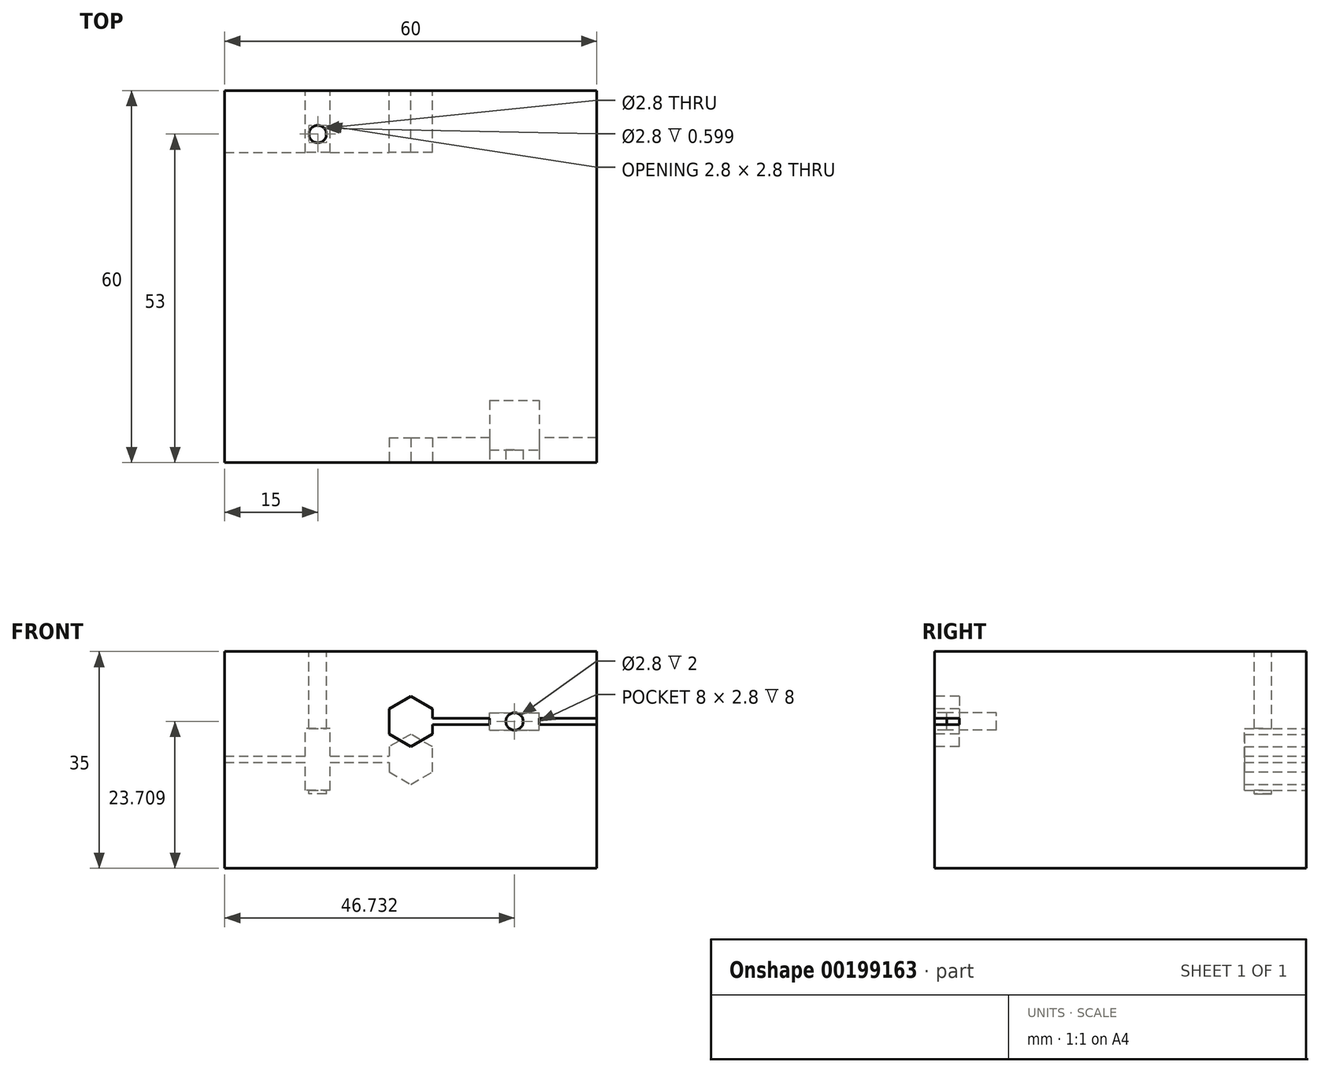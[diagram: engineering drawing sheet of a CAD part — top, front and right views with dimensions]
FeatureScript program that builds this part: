
annotation { "Feature Type Name" : "Feature", "Feature Type Description" : "" }
export const myFeature = defineFeature(function(context is Context, id is Id, definition is map)
    precondition{}
    {
        {
            var Q0;
            Q0=qCreatedBy(makeId("Top.planeOp"),FACE);
            var sketch = newSketch(context, id + "F0", { "sketchPlane" : qUnion([Q0])});
            skLineSegment(sketch, "E0.bottom", {"start": v(-30, -30) * mm, "end": v(30, -30) * mm});
            skLineSegment(sketch, "E0.top", {"start": v(-30, 30) * mm, "end": v(30, 30) * mm});
            skLineSegment(sketch, "E0.left", {"start": v(-30, -30) * mm, "end": v(-30, 30) * mm});
            skLineSegment(sketch, "E0.right", {"start": v(30, -30) * mm, "end": v(30, 30) * mm});
            skPoint(sketch, "E0.middle", {"position": v(0, 0) * mm});
            skSolve(sketch);
        }
        {
            var Q0;
            Q0=makeQuery(id+"F0.imprint","IMPRINT",FACE,{"disambiguationData":[TD([[makeQuery(id+"F0.imprint","IMPRINT",EDGE,{"derivedFrom":sQuery(id+"F0.wireOp",EDGE,"E0.bottom")}),1.0]])]});
            extrude(context, id + "F1", {"entities" : qUnion([Q0]), "depth" : 35 * mm});
        }
        {
            var Q0;
            Q0=makeQuery(id+"F1.opExtrude","SWEPT_FACE",FACE,{"disambiguationData":[OSD([sQuery(id+"F0.wireOp",EDGE,"E0.bottom")])]});
            var sketch = newSketch(context, id + "F2", { "sketchPlane" : qUnion([Q0])});
            skLineSegment(sketch, "E1.bottom", {"start": v(30, 24.2) * mm, "end": v(18.04, 24.2) * mm});
            skLineSegment(sketch, "E1.top", {"start": v(30, 23.2) * mm, "end": v(18.04, 23.2) * mm});
            skLineSegment(sketch, "E1.left", {"start": v(30, 24.2) * mm, "end": v(30, 23.2) * mm});
            skCircle(sketch, "E2", {"center": v(0, 23.7) * mm, "radius": 3.5 * mm});
            skCircle(sketch, "E3.cCircle", {"center": v(0, 23.7) * mm, "radius": 3.5 * mm, "construction": true});
            skLineSegment(sketch, "E3.0", {"start": v(-3.5, 21.69) * mm, "end": v(-3.5, 25.73) * mm});
            skLineSegment(sketch, "E3.1", {"start": v(-3.5, 25.73) * mm, "end": v(0, 27.75) * mm});
            skLineSegment(sketch, "E3.2", {"start": v(0, 27.75) * mm, "end": v(3.5, 25.73) * mm});
            skLineSegment(sketch, "E3.3", {"start": v(3.5, 25.73) * mm, "end": v(3.5, 21.69) * mm});
            skLineSegment(sketch, "E3.4", {"start": v(3.5, 21.69) * mm, "end": v(0, 19.67) * mm});
            skLineSegment(sketch, "E3.5", {"start": v(0, 19.67) * mm, "end": v(-3.5, 21.69) * mm});
            skPoint(sketch, "E3.0.midPoint", {"position": v(-3.5, 23.7) * mm});
            skCircle(sketch, "E4", {"center": v(16.73, 23.7) * mm, "radius": 1.4 * mm});
            skLineSegment(sketch, "E5.bottom", {"start": v(12.73, 22.3) * mm, "end": v(20.73, 22.3) * mm});
            skLineSegment(sketch, "E5.top", {"start": v(12.73, 25.1) * mm, "end": v(20.73, 25.1) * mm});
            skLineSegment(sketch, "E5.left", {"start": v(12.73, 22.3) * mm, "end": v(12.73, 25.1) * mm});
            skLineSegment(sketch, "E5.right", {"start": v(20.73, 22.3) * mm, "end": v(20.73, 25.1) * mm});
            skLineSegment(sketch, "E6.trimOffspring", {"start": v(15.42, 23.2) * mm, "end": v(3.46, 23.2) * mm});
            skLineSegment(sketch, "E7.trimOffspring", {"start": v(15.42, 24.2) * mm, "end": v(3.46, 24.2) * mm});
            skSolve(sketch);
        }
        {
            var Q0;
            {var subQ0=sQuery(id+"F2.wireOp",EDGE,"E7.trimOffspring");var subQ1=sQuery(id+"F2.wireOp",EDGE,"E4");var subQ2=makeQuery(id+"F2.imprint","INTERSECT",VERTEX,{"derivedFrom":[subQ1,subQ0]});Q0=makeQuery(id+"F2.imprint","IMPRINT",FACE,{"disambiguationData":[TD([[makeQuery(id+"F2.imprint","IMPRINT",EDGE,{"disambiguationData":[TD([[subQ2,1.0]])],"derivedFrom":subQ1}),-1.0]])]});}
            var Q1;
            {var subQ0=sQuery(id+"F2.wireOp",EDGE,"E6.trimOffspring");var subQ1=sQuery(id+"F2.wireOp",EDGE,"E4");var subQ2=makeQuery(id+"F2.imprint","INTERSECT",VERTEX,{"derivedFrom":[subQ1,subQ0]});Q1=makeQuery(id+"F2.imprint","IMPRINT",FACE,{"disambiguationData":[TD([[makeQuery(id+"F2.imprint","IMPRINT",EDGE,{"disambiguationData":[TD([[subQ2,1.0]])],"derivedFrom":subQ1}),-1.0]])]});}
            var Q2;
            {var subQ0=sQuery(id+"F2.wireOp",EDGE,"E6.trimOffspring");var subQ1=sQuery(id+"F2.wireOp",EDGE,"E4");var subQ2=makeQuery(id+"F2.imprint","INTERSECT",VERTEX,{"derivedFrom":[subQ1,subQ0]});Q2=makeQuery(id+"F2.imprint","IMPRINT",FACE,{"disambiguationData":[TD([[makeQuery(id+"F2.imprint","IMPRINT",EDGE,{"disambiguationData":[TD([[subQ2,-1.0]])],"derivedFrom":subQ1}),-1.0]])]});}
            var Q3;
            {var subQ0=sQuery(id+"F2.wireOp",EDGE,"E4");var subQ3=makeQuery(id+"F2.imprint","INTERSECT",VERTEX,{"derivedFrom":[sQuery(id+"F2.wireOp",EDGE,"E1.bottom"),subQ0]});Q3=makeQuery(id+"F2.imprint","IMPRINT",FACE,{"disambiguationData":[TD([[makeQuery(id+"F2.imprint","IMPRINT",EDGE,{"disambiguationData":[TD([[subQ3,-1.0]])],"derivedFrom":subQ0}),1.0]])]});}
            var Q4;
            {var subQ0=sQuery(id+"F2.wireOp",EDGE,"E4");var subQ1=sQuery(id+"F2.wireOp",EDGE,"E1.bottom");var subQ2=makeQuery(id+"F2.imprint","INTERSECT",VERTEX,{"derivedFrom":[subQ1,subQ0]});Q4=makeQuery(id+"F2.imprint","IMPRINT",FACE,{"disambiguationData":[TD([[makeQuery(id+"F2.imprint","IMPRINT",EDGE,{"disambiguationData":[TD([[subQ2,1.0]])],"derivedFrom":subQ1}),-1.0]])]});}
            var Q5;
            {var subQ0=sQuery(id+"F2.wireOp",EDGE,"E4");var subQ1=sQuery(id+"F2.wireOp",EDGE,"E1.bottom");var subQ2=makeQuery(id+"F2.imprint","INTERSECT",VERTEX,{"derivedFrom":[subQ1,subQ0]});Q5=makeQuery(id+"F2.imprint","IMPRINT",FACE,{"disambiguationData":[TD([[makeQuery(id+"F2.imprint","IMPRINT",EDGE,{"disambiguationData":[TD([[subQ2,1.0]])],"derivedFrom":subQ1}),1.0]])]});}
            var Q6;
            {var subQ0=sQuery(id+"F2.wireOp",EDGE,"E4");var subQ1=sQuery(id+"F2.wireOp",EDGE,"E1.top");var subQ2=makeQuery(id+"F2.imprint","INTERSECT",VERTEX,{"derivedFrom":[subQ1,subQ0]});Q6=makeQuery(id+"F2.imprint","IMPRINT",FACE,{"disambiguationData":[TD([[makeQuery(id+"F2.imprint","IMPRINT",EDGE,{"disambiguationData":[TD([[subQ2,1.0]])],"derivedFrom":subQ1}),1.0]])]});}
            extrude(context, id + "F3", {"entities" : qUnion([Q0, Q1, Q2, Q3, Q4, Q5, Q6]), "operationType" : NewBodyOperationType.REMOVE, "oppositeDirection" : true, "depth" : 10 * mm});
        }
        {
            var Q0;
            Q0 = qSketchRegion(id + "F2", true);
            extrude(context, id + "F4", {"entities" : qUnion([Q0]), "operationType" : NewBodyOperationType.REMOVE, "oppositeDirection" : true, "depth" : 4 * mm});
        }
        {
            var Q0;
            {var subQ0=sQuery(id+"F2.wireOp",EDGE,"E4");var subQ1=sQuery(id+"F2.wireOp",EDGE,"E1.top");var subQ2=makeQuery(id+"F2.imprint","INTERSECT",VERTEX,{"derivedFrom":[subQ1,subQ0]});Q0=makeQuery(id+"F2.imprint","IMPRINT",FACE,{"disambiguationData":[TD([[makeQuery(id+"F2.imprint","IMPRINT",EDGE,{"disambiguationData":[TD([[subQ2,1.0]])],"derivedFrom":subQ1}),1.0]])]});}
            var Q1;
            {var subQ0=sQuery(id+"F2.wireOp",EDGE,"E7.trimOffspring");var subQ1=sQuery(id+"F2.wireOp",EDGE,"E4");var subQ2=makeQuery(id+"F2.imprint","INTERSECT",VERTEX,{"derivedFrom":[subQ1,subQ0]});Q1=makeQuery(id+"F2.imprint","IMPRINT",FACE,{"disambiguationData":[TD([[makeQuery(id+"F2.imprint","IMPRINT",EDGE,{"disambiguationData":[TD([[subQ2,1.0]])],"derivedFrom":subQ1}),-1.0]])]});}
            var Q2;
            {var subQ0=sQuery(id+"F2.wireOp",EDGE,"E6.trimOffspring");var subQ1=sQuery(id+"F2.wireOp",EDGE,"E4");var subQ2=makeQuery(id+"F2.imprint","INTERSECT",VERTEX,{"derivedFrom":[subQ1,subQ0]});Q2=makeQuery(id+"F2.imprint","IMPRINT",FACE,{"disambiguationData":[TD([[makeQuery(id+"F2.imprint","IMPRINT",EDGE,{"disambiguationData":[TD([[subQ2,-1.0]])],"derivedFrom":subQ1}),-1.0]])]});}
            var Q3;
            {var subQ0=sQuery(id+"F2.wireOp",EDGE,"E4");var subQ1=sQuery(id+"F2.wireOp",EDGE,"E1.bottom");var subQ2=makeQuery(id+"F2.imprint","INTERSECT",VERTEX,{"derivedFrom":[subQ1,subQ0]});Q3=makeQuery(id+"F2.imprint","IMPRINT",FACE,{"disambiguationData":[TD([[makeQuery(id+"F2.imprint","IMPRINT",EDGE,{"disambiguationData":[TD([[subQ2,1.0]])],"derivedFrom":subQ1}),1.0]])]});}
            var Q4;
            {var subQ0=sQuery(id+"F2.wireOp",EDGE,"E6.trimOffspring");var subQ1=sQuery(id+"F2.wireOp",EDGE,"E4");var subQ2=makeQuery(id+"F2.imprint","INTERSECT",VERTEX,{"derivedFrom":[subQ1,subQ0]});Q4=makeQuery(id+"F2.imprint","IMPRINT",FACE,{"disambiguationData":[TD([[makeQuery(id+"F2.imprint","IMPRINT",EDGE,{"disambiguationData":[TD([[subQ2,1.0]])],"derivedFrom":subQ1}),-1.0]])]});}
            var Q5;
            {var subQ0=sQuery(id+"F2.wireOp",EDGE,"E4");var subQ1=sQuery(id+"F2.wireOp",EDGE,"E1.bottom");var subQ2=makeQuery(id+"F2.imprint","INTERSECT",VERTEX,{"derivedFrom":[subQ1,subQ0]});Q5=makeQuery(id+"F2.imprint","IMPRINT",FACE,{"disambiguationData":[TD([[makeQuery(id+"F2.imprint","IMPRINT",EDGE,{"disambiguationData":[TD([[subQ2,1.0]])],"derivedFrom":subQ1}),-1.0]])]});}
            extrude(context, id + "F5", {"entities" : qUnion([Q0, Q1, Q2, Q3, Q4, Q5]), "operationType" : NewBodyOperationType.ADD, "oppositeDirection" : true, "depth" : 2 * mm});
        }
        {
            var Q0;
            Q0=makeQuery(id+"F1.opExtrude","SWEPT_FACE",FACE,{"disambiguationData":[OSD([sQuery(id+"F0.wireOp",EDGE,"E0.top")])]});
            var sketch = newSketch(context, id + "F6", { "sketchPlane" : qUnion([Q0])});
            skPoint(sketch, "E8", {"position": v(15, 17.6) * mm});
            skLineSegment(sketch, "E9.bottom", {"start": v(30, 17.1) * mm, "end": v(0, 17.1) * mm});
            skLineSegment(sketch, "E9.top", {"start": v(30, 18.1) * mm, "end": v(0, 18.1) * mm});
            skLineSegment(sketch, "E9.left", {"start": v(30, 17.1) * mm, "end": v(30, 18.1) * mm});
            skLineSegment(sketch, "E9.right", {"start": v(0, 17.1) * mm, "end": v(0, 18.1) * mm});
            skCircle(sketch, "E10", {"center": v(0, 17.6) * mm, "radius": 3.5 * mm});
            skCircle(sketch, "E11.cCircle", {"center": v(0, 17.6) * mm, "radius": 3.5 * mm, "construction": true});
            skLineSegment(sketch, "E11.0", {"start": v(-3.5, 15.58) * mm, "end": v(-3.5, 19.62) * mm});
            skLineSegment(sketch, "E11.1", {"start": v(-3.5, 19.62) * mm, "end": v(0, 21.64) * mm});
            skLineSegment(sketch, "E11.2", {"start": v(0, 21.64) * mm, "end": v(3.5, 19.62) * mm});
            skLineSegment(sketch, "E11.3", {"start": v(3.5, 19.62) * mm, "end": v(3.5, 15.58) * mm});
            skLineSegment(sketch, "E11.4", {"start": v(3.5, 15.58) * mm, "end": v(0, 13.56) * mm});
            skLineSegment(sketch, "E11.5", {"start": v(0, 13.56) * mm, "end": v(-3.5, 15.58) * mm});
            skPoint(sketch, "E11.0.midPoint", {"position": v(-3.5, 17.6) * mm});
            skLineSegment(sketch, "E12.bottom", {"start": v(15.25, 18.1) * mm, "end": v(14.75, 18.1) * mm});
            skLineSegment(sketch, "E12.top", {"start": v(15.25, 35) * mm, "end": v(14.75, 35) * mm});
            skLineSegment(sketch, "E12.left", {"start": v(15.25, 18.1) * mm, "end": v(15.25, 35) * mm});
            skLineSegment(sketch, "E12.right", {"start": v(14.75, 18.1) * mm, "end": v(14.75, 35) * mm});
            skPoint(sketch, "E13.orphan", {"position": v(15, 35) * mm});
            skPoint(sketch, "E14.start.orphan", {"position": v(15, 18.1) * mm});
            skLineSegment(sketch, "E15", {"start": v(15, 17.6) * mm, "end": v(15, 12.6) * mm});
            skLineSegment(sketch, "E16.bottom", {"start": v(13, 12.6) * mm, "end": v(17, 12.6) * mm});
            skLineSegment(sketch, "E16.top", {"start": v(13, 17.6) * mm, "end": v(17, 17.6) * mm});
            skLineSegment(sketch, "E16.left", {"start": v(13, 12.6) * mm, "end": v(13, 17.6) * mm});
            skLineSegment(sketch, "E16.right", {"start": v(17, 12.6) * mm, "end": v(17, 17.6) * mm});
            skPoint(sketch, "E16.middle", {"position": v(15, 15.1) * mm});
            skLineSegment(sketch, "E17", {"start": v(14.75, 34.86) * mm, "end": v(15.25, 34.86) * mm});
            skLineSegment(sketch, "E18", {"start": v(15, 17.6) * mm, "end": v(15, 20.1) * mm});
            skLineSegment(sketch, "E19.top", {"start": v(13, 22.6) * mm, "end": v(17, 22.6) * mm});
            skLineSegment(sketch, "E19.left", {"start": v(13, 17.6) * mm, "end": v(13, 22.6) * mm});
            skLineSegment(sketch, "E19.right", {"start": v(17, 17.6) * mm, "end": v(17, 22.6) * mm});
            skPoint(sketch, "E19.middle", {"position": v(15, 20.1) * mm});
            skSolve(sketch);
        }
        {
            var Q0;
            {var subQ0=sQuery(id+"F6.wireOp",EDGE,"E11.2");var subQ1=sQuery(id+"F6.wireOp",EDGE,"E10");var subQ2=makeQuery(id+"F6.imprint","INTERSECT",VERTEX,{"derivedFrom":[subQ1,subQ0]});Q0=makeQuery(id+"F6.imprint","IMPRINT",FACE,{"disambiguationData":[TD([[makeQuery(id+"F6.imprint","IMPRINT",EDGE,{"disambiguationData":[TD([[subQ2,-1.0]])],"derivedFrom":subQ1}),-1.0]])]});}
            var Q1;
            {var subQ0=sQuery(id+"F6.wireOp",EDGE,"E11.1");var subQ1=sQuery(id+"F6.wireOp",EDGE,"E10");var subQ2=makeQuery(id+"F6.imprint","INTERSECT",VERTEX,{"derivedFrom":[subQ1,subQ0]});Q1=makeQuery(id+"F6.imprint","IMPRINT",FACE,{"disambiguationData":[TD([[makeQuery(id+"F6.imprint","IMPRINT",EDGE,{"disambiguationData":[TD([[subQ2,-1.0]])],"derivedFrom":subQ1}),-1.0]])]});}
            var Q2;
            {var subQ0=sQuery(id+"F6.wireOp",EDGE,"E11.0");var subQ1=sQuery(id+"F6.wireOp",EDGE,"E10");var subQ2=makeQuery(id+"F6.imprint","INTERSECT",VERTEX,{"derivedFrom":[subQ1,subQ0]});Q2=makeQuery(id+"F6.imprint","IMPRINT",FACE,{"disambiguationData":[TD([[makeQuery(id+"F6.imprint","IMPRINT",EDGE,{"disambiguationData":[TD([[subQ2,-1.0]])],"derivedFrom":subQ1}),-1.0]])]});}
            var Q3;
            {var subQ0=sQuery(id+"F6.wireOp",EDGE,"E11.5");var subQ1=sQuery(id+"F6.wireOp",EDGE,"E10");var subQ2=makeQuery(id+"F6.imprint","INTERSECT",VERTEX,{"derivedFrom":[subQ1,subQ0]});Q3=makeQuery(id+"F6.imprint","IMPRINT",FACE,{"disambiguationData":[TD([[makeQuery(id+"F6.imprint","IMPRINT",EDGE,{"disambiguationData":[TD([[subQ2,-1.0]])],"derivedFrom":subQ1}),-1.0]])]});}
            var Q4;
            {var subQ0=sQuery(id+"F6.wireOp",EDGE,"E11.3");var subQ1=sQuery(id+"F6.wireOp",EDGE,"E9.bottom");var subQ2=makeQuery(id+"F6.imprint","INTERSECT",VERTEX,{"derivedFrom":[subQ1,subQ0]});Q4=makeQuery(id+"F6.imprint","IMPRINT",FACE,{"disambiguationData":[TD([[makeQuery(id+"F6.imprint","IMPRINT",EDGE,{"disambiguationData":[TD([[subQ2,-1.0]])],"derivedFrom":subQ1}),1.0]])]});}
            var Q5;
            {var subQ0=sQuery(id+"F6.wireOp",EDGE,"E11.3");var subQ1=sQuery(id+"F6.wireOp",EDGE,"E9.bottom");var subQ2=makeQuery(id+"F6.imprint","INTERSECT",VERTEX,{"derivedFrom":[subQ1,subQ0]});Q5=makeQuery(id+"F6.imprint","IMPRINT",FACE,{"disambiguationData":[TD([[makeQuery(id+"F6.imprint","IMPRINT",EDGE,{"disambiguationData":[TD([[subQ2,-1.0]])],"derivedFrom":subQ1}),-1.0]])]});}
            var Q6;
            {var subQ0=sQuery(id+"F6.wireOp",EDGE,"E11.3");var subQ1=sQuery(id+"F6.wireOp",EDGE,"E9.top");var subQ2=makeQuery(id+"F6.imprint","INTERSECT",VERTEX,{"derivedFrom":[subQ1,subQ0]});Q6=makeQuery(id+"F6.imprint","IMPRINT",FACE,{"disambiguationData":[TD([[makeQuery(id+"F6.imprint","IMPRINT",EDGE,{"disambiguationData":[TD([[subQ2,-1.0]])],"derivedFrom":subQ1}),1.0]])]});}
            var Q7;
            {var subQ0=sQuery(id+"F6.wireOp",EDGE,"E11.3");var subQ1=sQuery(id+"F6.wireOp",EDGE,"E9.top");var subQ2=makeQuery(id+"F6.imprint","INTERSECT",VERTEX,{"derivedFrom":[subQ1,subQ0]});Q7=makeQuery(id+"F6.imprint","IMPRINT",FACE,{"disambiguationData":[TD([[makeQuery(id+"F6.imprint","IMPRINT",EDGE,{"disambiguationData":[TD([[subQ2,-1.0]])],"derivedFrom":subQ1}),-1.0]])]});}
            var Q8;
            {var subQ0=sQuery(id+"F6.wireOp",EDGE,"E9.left");Q8=makeQuery(id+"F6.imprint","IMPRINT",FACE,{"disambiguationData":[TD([[makeQuery(id+"F6.imprint","IMPRINT",EDGE,{"derivedFrom":subQ0}),-1.0]])]});}
            var Q9;
            {var subQ7=sQuery(id+"F6.wireOp",EDGE,"E9.right");Q9=makeQuery(id+"F6.imprint","IMPRINT",FACE,{"disambiguationData":[TD([[makeQuery(id+"F6.imprint","IMPRINT",EDGE,{"derivedFrom":subQ7}),1.0]])]});}
            var Q10;
            {var subQ0=sQuery(id+"F6.wireOp",EDGE,"E15");var subQ1=sQuery(id+"F6.wireOp",EDGE,"E9.bottom");var subQ2=makeQuery(id+"F6.imprint","INTERSECT",VERTEX,{"derivedFrom":[subQ1,subQ0]});Q10=makeQuery(id+"F6.imprint","IMPRINT",FACE,{"disambiguationData":[TD([[makeQuery(id+"F6.imprint","IMPRINT",EDGE,{"disambiguationData":[TD([[subQ2,-1.0]])],"derivedFrom":subQ1}),-1.0]])]});}
            var Q11;
            {var subQ0=sQuery(id+"F6.wireOp",EDGE,"E16.right");var subQ1=sQuery(id+"F6.wireOp",EDGE,"E9.bottom");var subQ2=makeQuery(id+"F6.imprint","INTERSECT",VERTEX,{"derivedFrom":[subQ1,subQ0]});Q11=makeQuery(id+"F6.imprint","IMPRINT",FACE,{"disambiguationData":[TD([[makeQuery(id+"F6.imprint","IMPRINT",EDGE,{"disambiguationData":[TD([[subQ2,-1.0]])],"derivedFrom":subQ1}),-1.0]])]});}
            var Q12;
            {var subQ0=sQuery(id+"F6.wireOp",EDGE,"E16.right");var subQ1=sQuery(id+"F6.wireOp",EDGE,"E9.bottom");var subQ2=makeQuery(id+"F6.imprint","INTERSECT",VERTEX,{"derivedFrom":[subQ1,subQ0]});Q12=makeQuery(id+"F6.imprint","IMPRINT",FACE,{"disambiguationData":[TD([[makeQuery(id+"F6.imprint","IMPRINT",EDGE,{"disambiguationData":[TD([[subQ2,-1.0]])],"derivedFrom":subQ1}),1.0]])]});}
            var Q13;
            {var subQ0=sQuery(id+"F6.wireOp",EDGE,"E15");var subQ1=sQuery(id+"F6.wireOp",EDGE,"E9.bottom");var subQ2=makeQuery(id+"F6.imprint","INTERSECT",VERTEX,{"derivedFrom":[subQ1,subQ0]});Q13=makeQuery(id+"F6.imprint","IMPRINT",FACE,{"disambiguationData":[TD([[makeQuery(id+"F6.imprint","IMPRINT",EDGE,{"disambiguationData":[TD([[subQ2,-1.0]])],"derivedFrom":subQ1}),1.0]])]});}
            var Q14;
            {var subQ4=sQuery(id+"F6.wireOp",EDGE,"E9.right");Q14=makeQuery(id+"F6.imprint","IMPRINT",FACE,{"disambiguationData":[TD([[makeQuery(id+"F6.imprint","IMPRINT",EDGE,{"derivedFrom":subQ4}),-1.0]])]});}
            var Q15;
            {var subQ4=sQuery(id+"F6.wireOp",EDGE,"E19.top");var subQ7=sQuery(id+"F6.wireOp",EDGE,"E12.left");var subQ9=makeQuery(id+"F6.imprint","INTERSECT",VERTEX,{"derivedFrom":[subQ7,subQ4]});Q15=makeQuery(id+"F6.imprint","IMPRINT",FACE,{"disambiguationData":[TD([[makeQuery(id+"F6.imprint","IMPRINT",EDGE,{"disambiguationData":[TD([[subQ9,1.0]])],"derivedFrom":subQ4}),-1.0]])]});}
            var Q16;
            {var subQ3=sQuery(id+"F6.wireOp",EDGE,"E19.left");var subQ5=sQuery(id+"F6.wireOp",EDGE,"E19.top");var subQ7=makeQuery(id+"F6.imprint","INTERSECT",VERTEX,{"derivedFrom":[subQ5,subQ3]});Q16=makeQuery(id+"F6.imprint","IMPRINT",FACE,{"disambiguationData":[TD([[makeQuery(id+"F6.imprint","IMPRINT",EDGE,{"disambiguationData":[TD([[subQ7,-1.0]])],"derivedFrom":subQ5}),-1.0]])]});}
            var Q17;
            {var subQ3=sQuery(id+"F6.wireOp",EDGE,"E19.right");var subQ5=sQuery(id+"F6.wireOp",EDGE,"E19.top");var subQ7=makeQuery(id+"F6.imprint","INTERSECT",VERTEX,{"derivedFrom":[subQ5,subQ3]});Q17=makeQuery(id+"F6.imprint","IMPRINT",FACE,{"disambiguationData":[TD([[makeQuery(id+"F6.imprint","IMPRINT",EDGE,{"disambiguationData":[TD([[subQ7,1.0]])],"derivedFrom":subQ5}),-1.0]])]});}
            var Q18;
            {var subQ3=sQuery(id+"F6.wireOp",EDGE,"E19.left");var subQ7=sQuery(id+"F6.wireOp",EDGE,"E9.top");var subQ9=makeQuery(id+"F6.imprint","INTERSECT",VERTEX,{"derivedFrom":[subQ7,subQ3]});Q18=makeQuery(id+"F6.imprint","IMPRINT",FACE,{"disambiguationData":[TD([[makeQuery(id+"F6.imprint","IMPRINT",EDGE,{"disambiguationData":[TD([[subQ9,1.0]])],"derivedFrom":subQ7}),1.0]])]});}
            var Q19;
            {var subQ3=sQuery(id+"F6.wireOp",EDGE,"E19.right");var subQ6=sQuery(id+"F6.wireOp",EDGE,"E9.top");var subQ9=makeQuery(id+"F6.imprint","INTERSECT",VERTEX,{"derivedFrom":[subQ6,subQ3]});Q19=makeQuery(id+"F6.imprint","IMPRINT",FACE,{"disambiguationData":[TD([[makeQuery(id+"F6.imprint","IMPRINT",EDGE,{"disambiguationData":[TD([[subQ9,-1.0]])],"derivedFrom":subQ6}),1.0]])]});}
            var Q20;
            {var subQ1=sQuery(id+"F6.wireOp",EDGE,"E9.bottom");var subQ8=sQuery(id+"F6.wireOp",EDGE,"E16.left");var subQ9=makeQuery(id+"F6.imprint","INTERSECT",VERTEX,{"derivedFrom":[subQ1,subQ8]});Q20=makeQuery(id+"F6.imprint","IMPRINT",FACE,{"disambiguationData":[TD([[makeQuery(id+"F6.imprint","IMPRINT",EDGE,{"disambiguationData":[TD([[subQ9,-1.0]])],"derivedFrom":subQ1}),-1.0]])]});}
            extrude(context, id + "F7", {"entities" : qUnion([Q0, Q1, Q2, Q3, Q4, Q5, Q6, Q7, Q8, Q9, Q10, Q11, Q12, Q13, Q14, Q15, Q16, Q17, Q18, Q19, Q20]), "operationType" : NewBodyOperationType.REMOVE, "oppositeDirection" : true, "depth" : 10 * mm});
        }
        {
            var Q0;
            Q0=makeQuery(id+"F1.opExtrude","CAP_FACE",FACE,{"disambiguationData":[OSD([sQuery(id+"F0.wireOp",EDGE,"E0.bottom"),sQuery(id+"F0.wireOp",EDGE,"E0.top"),sQuery(id+"F0.wireOp",EDGE,"E0.left"),sQuery(id+"F0.wireOp",EDGE,"E0.right")])],"isStart":false});
            var sketch = newSketch(context, id + "F8", { "sketchPlane" : qUnion([Q0])});
            skLineSegment(sketch, "E20", {"start": v(-30, 30) * mm, "end": v(-30, 30) * mm});
            skLineSegment(sketch, "E21", {"start": v(-30, 30) * mm, "end": v(-15, 30) * mm});
            skLineSegment(sketch, "E22", {"start": v(-15, 30) * mm, "end": v(-15, 20) * mm});
            skPoint(sketch, "E23", {"position": v(-15, 23) * mm});
            skCircle(sketch, "E24", {"center": v(-15, 23) * mm, "radius": 1.4 * mm});
            skSolve(sketch);
        }
        {
            var Q0;
            Q0 = qSketchRegion(id + "F8", true);
            extrude(context, id + "F9", {"entities" : qUnion([Q0]), "operationType" : NewBodyOperationType.REMOVE, "oppositeDirection" : true, "depth" : 23 * mm});
        }
    });
